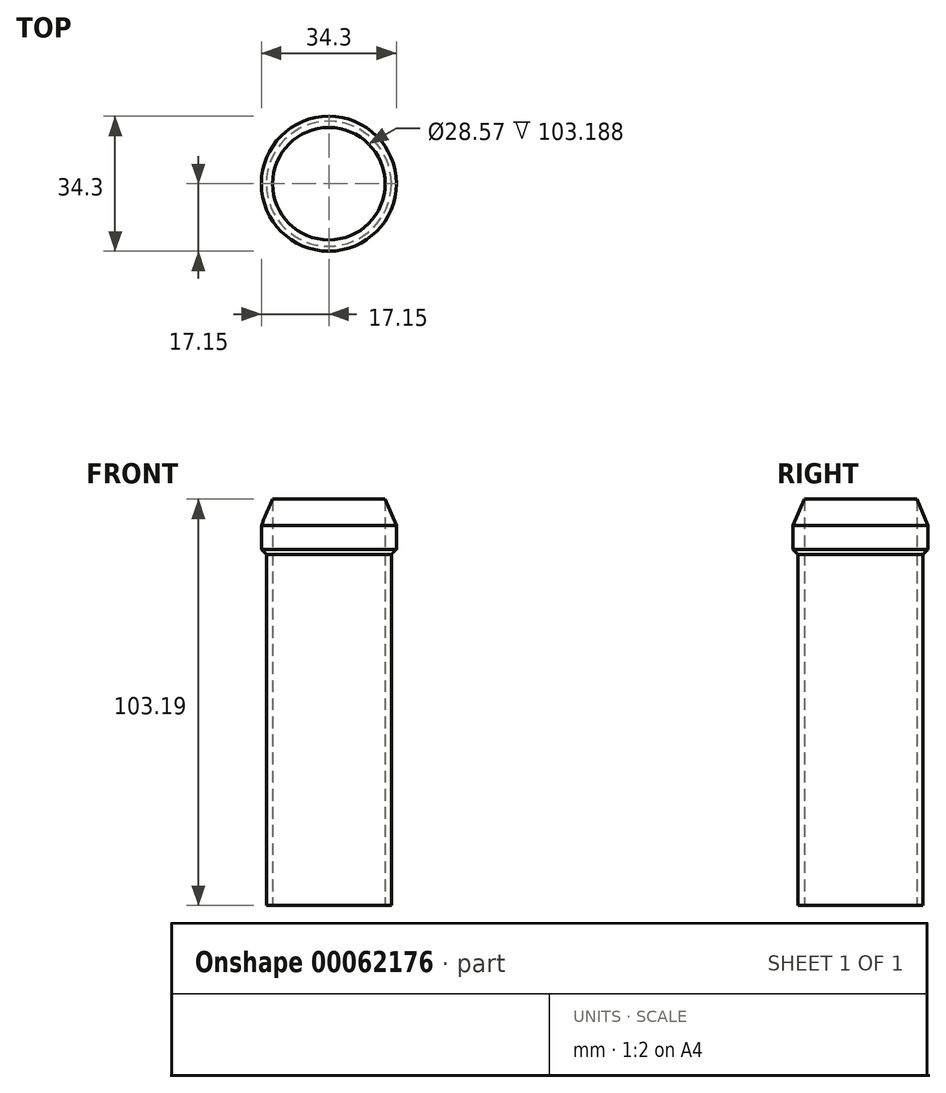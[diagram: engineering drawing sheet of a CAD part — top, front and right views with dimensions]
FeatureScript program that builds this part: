
annotation { "Feature Type Name" : "Feature", "Feature Type Description" : "" }
export const myFeature = defineFeature(function(context is Context, id is Id, definition is map)
    precondition{}
    {
        {
            var Q0;
            Q0=qCreatedBy(makeId("Top.planeOp"),FACE);
            var sketch = newSketch(context, id + "F0", { "sketchPlane" : qUnion([Q0])});
            skCircle(sketch, "E0", {"center": v(0, 0) * mm, "radius": 15.88 * mm});
            skCircle(sketch, "E1", {"center": v(0, 0) * mm, "radius": 14.29 * mm});
            skSolve(sketch);
        }
        {
            var Q0;
            Q0 = qSketchRegion(id + "F0", true);
            extrude(context, id + "F1", {"entities" : qUnion([Q0]), "endBound" : BoundingType.SYMMETRIC, "depth" : 88.9 * mm});
        }
        {
            var Q0;
            Q0=makeQuery(id+"F1.opExtrude","CAP_FACE",FACE,{"disambiguationData":[OSD([sQuery(id+"F0.wireOp",EDGE,"E0"),sQuery(id+"F0.wireOp",EDGE,"E1")])],"isStart":false});
            var sketch = newSketch(context, id + "F2", { "sketchPlane" : qUnion([Q0])});
            skCircle(sketch, "E2", {"center": v(0, 0) * mm, "radius": 14.29 * mm});
            skCircle(sketch, "E3", {"center": v(0, 0) * mm, "radius": 17.15 * mm});
            skSolve(sketch);
        }
        {
            var Q0;
            Q0 = qSketchRegion(id + "F2", true);
            extrude(context, id + "F3", {"entities" : qUnion([Q0]), "operationType" : NewBodyOperationType.ADD, "depth" : 16.5 * mm});
        }
        {
            var Q0;
            Q0=makeQuery(id+"F3.opExtrude","CAP_EDGE",EDGE,{"disambiguationData":[OSD([sQuery(id+"F2.wireOp",EDGE,"E3")])],"isStart":false});
            chamfer(context, id + "F4", {"entities" : qUnion([Q0]), "chamferType" : ChamferType.TWO_OFFSETS, "width1" : 3.8 * mm, "oppositeDirection" : false, "width2" : 8.9 * mm, "tangentPropagation" : true});
        }
        {
            var Q0;
            Q0=makeQuery(id+"F3.opExtrude","CAP_EDGE",EDGE,{"disambiguationData":[OSD([sQuery(id+"F2.wireOp",EDGE,"E3")])],"isStart":true});
            chamfer(context, id + "F5", {"entities" : qUnion([Q0]), "width" : 1.52 * mm, "tangentPropagation" : true});
        }
    });
